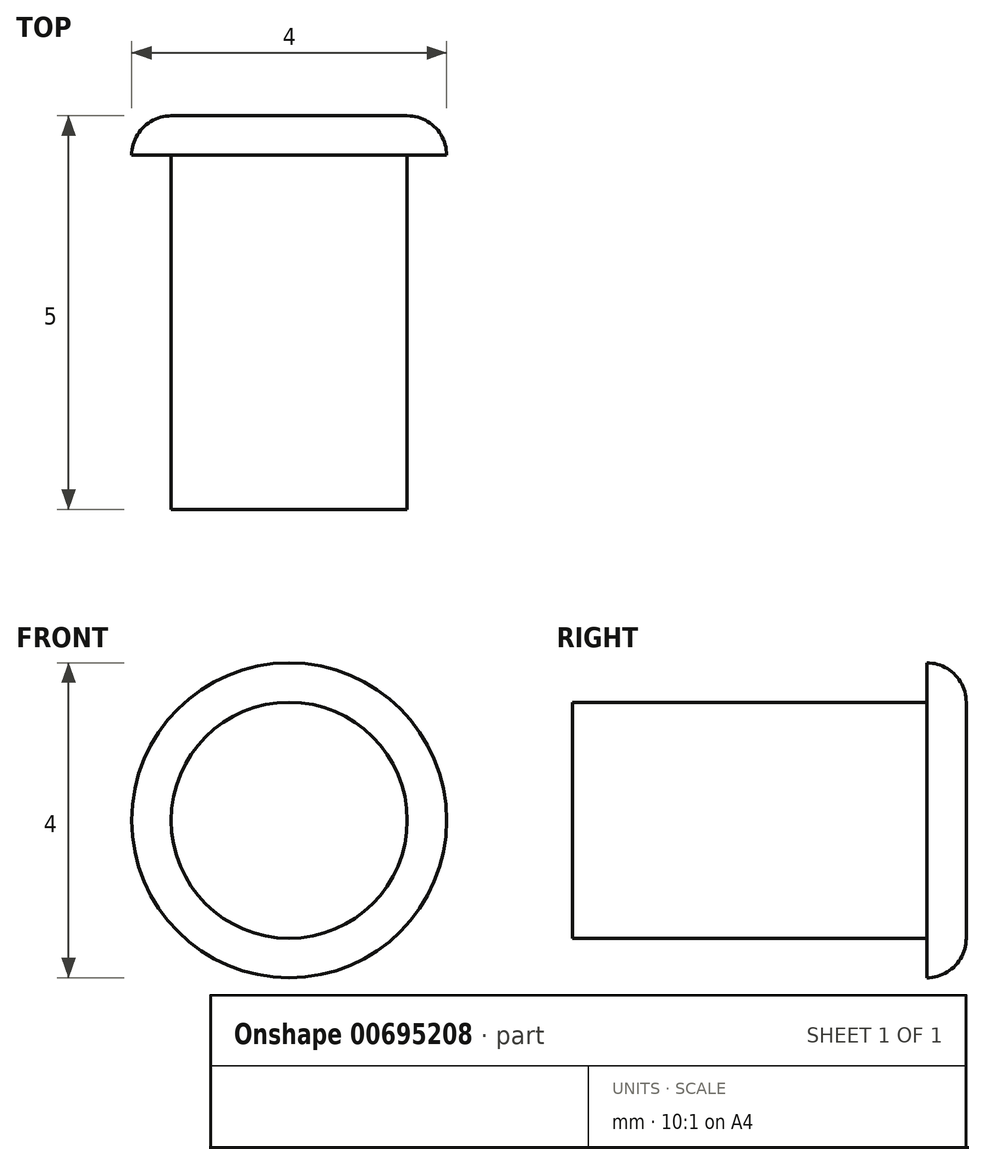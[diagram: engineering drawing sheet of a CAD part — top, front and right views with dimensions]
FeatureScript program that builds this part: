
annotation { "Feature Type Name" : "Feature", "Feature Type Description" : "" }
export const myFeature = defineFeature(function(context is Context, id is Id, definition is map)
    precondition{}
    {
        {
            var Q0;
            Q0=qCreatedBy(makeId("Top.planeOp"),FACE);
            var sketch = newSketch(context, id + "F0", { "sketchPlane" : qUnion([Q0])});
            skLineSegment(sketch, "E0.bottom", {"start": v(0, 0) * mm, "end": v(-1.5, 0) * mm});
            skLineSegment(sketch, "E0.right", {"start": v(-1.5, 0) * mm, "end": v(-1.5, 4.5) * mm});
            skLineSegment(sketch, "E1", {"start": v(-1.5, 4.5) * mm, "end": v(-2, 4.5) * mm});
            skArc(sketch, "E2", {"start": v(-1.5, 5) * mm, "mid": v(-1.85, 4.85) * mm, "end": v(-2, 4.5) * mm});
            skLineSegment(sketch, "E3", {"start": v(-1.5, 5) * mm, "end": v(0.79, 5) * mm});
            skLineSegment(sketch, "E4", {"start": v(0, 0) * mm, "end": v(0, 5.47) * mm});
            skSolve(sketch);
        }
        {
            var Q0;
            {var subQ1=sQuery(id+"F0.wireOp",EDGE,"E0.bottom");Q0=makeQuery(id+"F0.imprint","IMPRINT",FACE,{"disambiguationData":[TD([[makeQuery(id+"F0.imprint","IMPRINT",EDGE,{"derivedFrom":subQ1}),-1.0]])]});}
            var Q1;
            Q1=sQuery(id+"F0.wireOp",EDGE,"E4");
            revolve(context, id + "F1", {"entities" : qUnion([Q0]), "axis" : qUnion([Q1]), "revolveType" : RevolveType.FULL});
        }
    });
